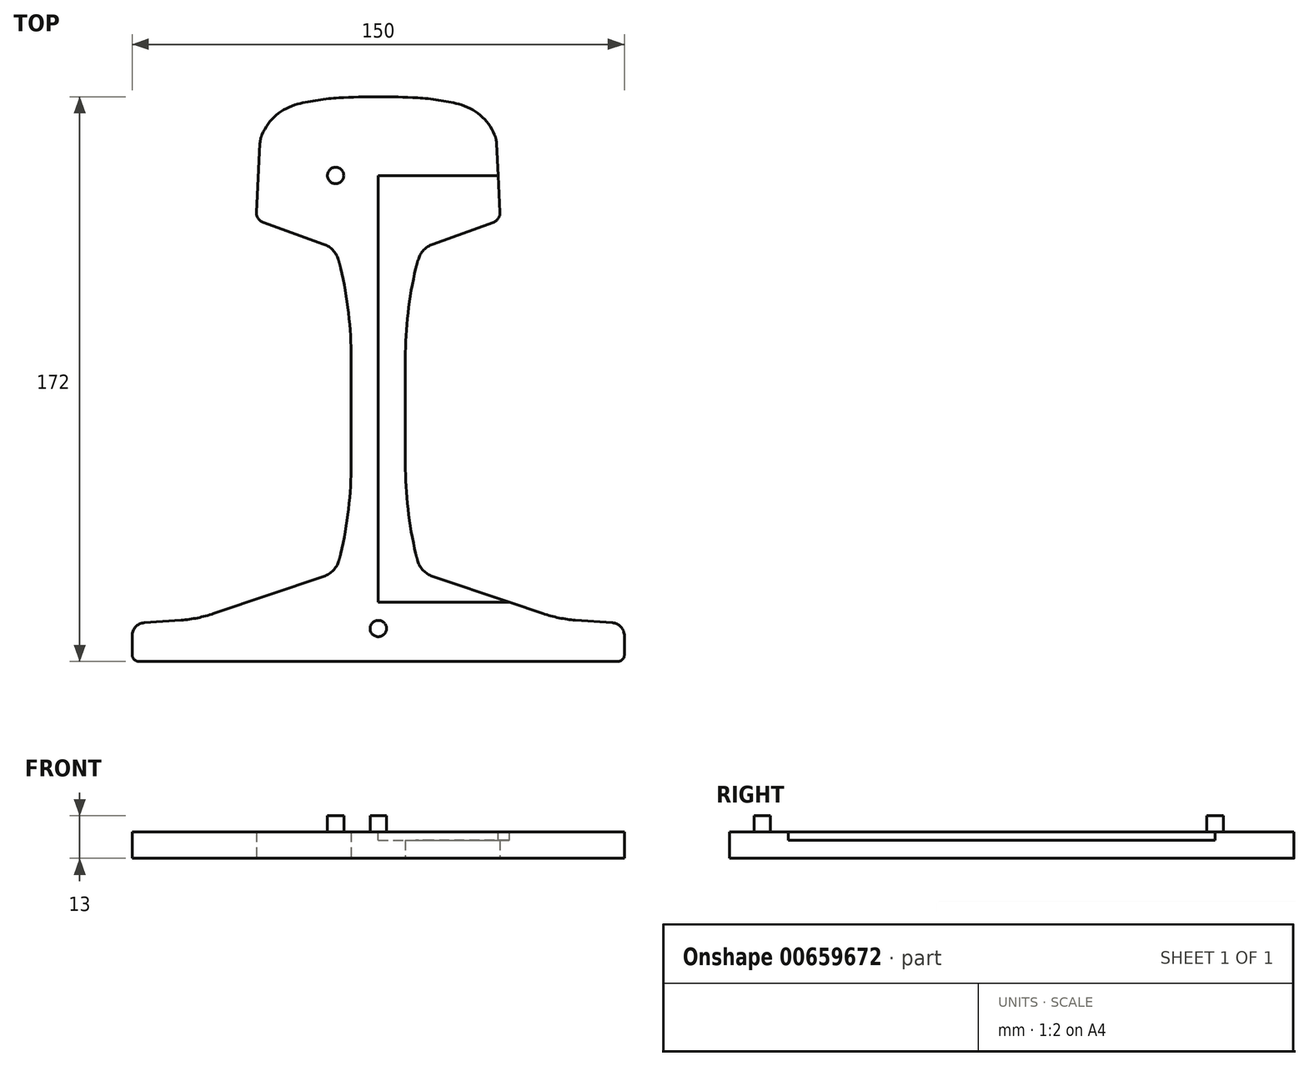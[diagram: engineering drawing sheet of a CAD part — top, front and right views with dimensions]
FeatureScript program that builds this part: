
annotation { "Feature Type Name" : "Feature", "Feature Type Description" : "" }
export const myFeature = defineFeature(function(context is Context, id is Id, definition is map)
    precondition{}
    {
        {
            var Q0;
            Q0=qCreatedBy(makeId("Top.planeOp"),FACE);
            var sketch = newSketch(context, id + "F0", { "sketchPlane" : qUnion([Q0])});
            skPoint(sketch, "E0.middle", {"position": v(0, 0) * mm});
            skLineSegment(sketch, "E1", {"start": v(0, 0) * mm, "end": v(73, 0) * mm});
            skLineSegment(sketch, "E2", {"start": v(75, 2) * mm, "end": v(75, 7.78) * mm});
            skLineSegment(sketch, "E3", {"start": v(0, 0) * mm, "end": v(0, 172) * mm, "construction": true});
            skLineSegment(sketch, "E4", {"start": v(71.28, 11.77) * mm, "end": v(60.1, 12.56) * mm});
            skLineSegment(sketch, "E5", {"start": v(50.15, 14.56) * mm, "end": v(16.5, 25.93) * mm});
            skPoint(sketch, "E6.orphan", {"position": v(0, 16.86) * mm});
            skPoint(sketch, "E7.visualSharp", {"position": v(75, 11.5) * mm});
            skArc(sketch, "E7.filletArc", {"start": v(75, 7.78) * mm, "mid": v(73.93, 10.5) * mm, "end": v(71.28, 11.77) * mm});
            skPoint(sketch, "E8.visualSharp", {"position": v(75, 0) * mm});
            skArc(sketch, "E8.filletArc", {"start": v(73, 0) * mm, "mid": v(74.41, 0.59) * mm, "end": v(75, 2) * mm});
            skPoint(sketch, "E9.visualSharp", {"position": v(55, 12.93) * mm});
            skArc(sketch, "E9.filletArc", {"start": v(50.15, 14.56) * mm, "mid": v(55.06, 13.25) * mm, "end": v(60.1, 12.56) * mm});
            skArc(sketch, "E10", {"start": v(8.25, 60.25) * mm, "mid": v(9.05, 46.4) * mm, "end": v(11.45, 32.72) * mm});
            skArc(sketch, "E11", {"start": v(11.45, 32.72) * mm, "mid": v(11.73, 31.61) * mm, "end": v(12.05, 30.51) * mm});
            skPoint(sketch, "E12.orphan", {"position": v(0, 31.5) * mm});
            skLineSegment(sketch, "E13", {"start": v(16.5, 127) * mm, "end": v(35.13, 133.78) * mm});
            skLineSegment(sketch, "E14", {"start": v(37.1, 136.75) * mm, "end": v(36.06, 157.7) * mm});
            skLineSegment(sketch, "E15", {"start": v(37.22, 134.53) * mm, "end": v(37.22, 152.14) * mm, "construction": true});
            skArc(sketch, "E16", {"start": v(24.5, 169.74) * mm, "mid": v(31.09, 166.37) * mm, "end": v(35.44, 160.4) * mm});
            skLineSegment(sketch, "E17", {"start": v(0, 172) * mm, "end": v(-54.44, 172) * mm, "construction": true});
            skArc(sketch, "E18", {"start": v(12, 171.64) * mm, "mid": v(6, 171.9) * mm, "end": v(0, 172) * mm});
            skArc(sketch, "E19", {"start": v(12, 171.64) * mm, "mid": v(18.3, 170.97) * mm, "end": v(24.5, 169.74) * mm});
            skPoint(sketch, "E20.visualSharp", {"position": v(36, 158.86) * mm});
            skArc(sketch, "E20.filletArc", {"start": v(36.06, 157.7) * mm, "mid": v(35.87, 159.07) * mm, "end": v(35.44, 160.4) * mm});
            skPoint(sketch, "E21.visualSharp", {"position": v(37.22, 134.53) * mm});
            skArc(sketch, "E22", {"start": v(11.45, 119.78) * mm, "mid": v(9.05, 106.1) * mm, "end": v(8.25, 92.25) * mm});
            skLineSegment(sketch, "E23", {"start": v(0, 121) * mm, "end": v(67.7, 121) * mm, "construction": true});
            skArc(sketch, "E24.filletArc", {"start": v(35.13, 133.78) * mm, "mid": v(36.6, 134.94) * mm, "end": v(37.1, 136.75) * mm});
            skArc(sketch, "E25", {"start": v(12.24, 122.6) * mm, "mid": v(11.81, 121.2) * mm, "end": v(11.45, 119.78) * mm});
            skPoint(sketch, "E26.visualSharp", {"position": v(13.51, 125.91) * mm});
            skArc(sketch, "E26.filletArc", {"start": v(16.5, 127) * mm, "mid": v(13.86, 125.29) * mm, "end": v(12.24, 122.6) * mm});
            skLineSegment(sketch, "E27", {"start": v(8.25, 92.25) * mm, "end": v(8.25, 60.25) * mm});
            skArc(sketch, "E28.MirrorCS", {"start": v(-12, 171.64) * mm, "mid": v(-18.3, 170.97) * mm, "end": v(-24.5, 169.74) * mm});
            skArc(sketch, "E29.MirrorCS", {"start": v(-12, 171.64) * mm, "mid": v(-6, 171.9) * mm, "end": v(0, 172) * mm});
            skArc(sketch, "E30.MirrorCS", {"start": v(-24.5, 169.74) * mm, "mid": v(-31.09, 166.37) * mm, "end": v(-35.44, 160.4) * mm});
            skArc(sketch, "E31.MirrorCS", {"start": v(-36.06, 157.7) * mm, "mid": v(-35.87, 159.07) * mm, "end": v(-35.44, 160.4) * mm});
            skLineSegment(sketch, "E32.MirrorCS", {"start": v(-37.1, 136.75) * mm, "end": v(-36.06, 157.7) * mm});
            skArc(sketch, "E33.MirrorCS", {"start": v(-35.13, 133.78) * mm, "mid": v(-36.6, 134.94) * mm, "end": v(-37.1, 136.75) * mm});
            skLineSegment(sketch, "E34.MirrorCS", {"start": v(-16.5, 127) * mm, "end": v(-35.13, 133.78) * mm});
            skArc(sketch, "E35.MirrorCS", {"start": v(-16.5, 127) * mm, "mid": v(-13.86, 125.29) * mm, "end": v(-12.24, 122.6) * mm});
            skArc(sketch, "E36.MirrorCS", {"start": v(-12.24, 122.6) * mm, "mid": v(-11.81, 121.2) * mm, "end": v(-11.45, 119.78) * mm});
            skArc(sketch, "E37.MirrorCS", {"start": v(-11.45, 119.78) * mm, "mid": v(-9.05, 106.1) * mm, "end": v(-8.25, 92.25) * mm});
            skLineSegment(sketch, "E38.MirrorCS", {"start": v(-8.25, 92.25) * mm, "end": v(-8.25, 60.25) * mm});
            skArc(sketch, "E39.MirrorCS", {"start": v(-8.25, 60.25) * mm, "mid": v(-9.05, 46.4) * mm, "end": v(-11.45, 32.72) * mm});
            skArc(sketch, "E40.MirrorCS", {"start": v(-11.45, 32.72) * mm, "mid": v(-11.73, 31.61) * mm, "end": v(-12.05, 30.51) * mm});
            skLineSegment(sketch, "E41.MirrorCS", {"start": v(-50.15, 14.56) * mm, "end": v(-16.5, 25.93) * mm});
            skArc(sketch, "E42.MirrorCS", {"start": v(-50.15, 14.56) * mm, "mid": v(-55.06, 13.25) * mm, "end": v(-60.1, 12.56) * mm});
            skLineSegment(sketch, "E43.MirrorCS", {"start": v(-71.28, 11.77) * mm, "end": v(-60.1, 12.56) * mm});
            skPoint(sketch, "E44.MirrorP", {"position": v(-75, 11.5) * mm});
            skArc(sketch, "E45.MirrorCS", {"start": v(-75, 7.78) * mm, "mid": v(-73.93, 10.5) * mm, "end": v(-71.28, 11.77) * mm});
            skLineSegment(sketch, "E46.MirrorCS", {"start": v(-75, 2) * mm, "end": v(-75, 7.78) * mm});
            skArc(sketch, "E47.MirrorCS", {"start": v(-73, 0) * mm, "mid": v(-74.41, 0.59) * mm, "end": v(-75, 2) * mm});
            skLineSegment(sketch, "E48.MirrorCS", {"start": v(0, 0) * mm, "end": v(-73, 0) * mm});
            skPoint(sketch, "E49.visualSharp", {"position": v(13.33, 27) * mm});
            skArc(sketch, "E49.filletArc", {"start": v(12.05, 30.51) * mm, "mid": v(13.72, 27.68) * mm, "end": v(16.5, 25.93) * mm});
            skPoint(sketch, "E50.visualSharp", {"position": v(-13.33, 27) * mm});
            skArc(sketch, "E50.filletArc", {"start": v(-16.5, 25.93) * mm, "mid": v(-13.72, 27.68) * mm, "end": v(-12.05, 30.51) * mm});
            skSolve(sketch);
        }
        {
            var Q0;
            Q0=makeQuery(id+"F0.imprint","IMPRINT",FACE,{"disambiguationData":[TD([[makeQuery(id+"F0.imprint","IMPRINT",EDGE,{"derivedFrom":sQuery(id+"F0.wireOp",EDGE,"E1")}),1.0]])]});
            extrude(context, id + "F1", {"entities" : qUnion([Q0]), "depth" : 8 * mm, "offsetDistance" : 25 * mm});
        }
        {
            var Q0;
            Q0=makeQuery(id+"F1.opExtrude","CAP_FACE",FACE,{"disambiguationData":[OSD([sQuery(id+"F0.wireOp",EDGE,"E1"),sQuery(id+"F0.wireOp",EDGE,"E2"),sQuery(id+"F0.wireOp",EDGE,"E4"),sQuery(id+"F0.wireOp",EDGE,"E5"),sQuery(id+"F0.wireOp",EDGE,"E7.filletArc"),sQuery(id+"F0.wireOp",EDGE,"E8.filletArc"),sQuery(id+"F0.wireOp",EDGE,"E9.filletArc"),sQuery(id+"F0.wireOp",EDGE,"E10"),sQuery(id+"F0.wireOp",EDGE,"E11"),sQuery(id+"F0.wireOp",EDGE,"E13"),sQuery(id+"F0.wireOp",EDGE,"E14"),sQuery(id+"F0.wireOp",EDGE,"E16"),sQuery(id+"F0.wireOp",EDGE,"E18"),sQuery(id+"F0.wireOp",EDGE,"E19"),sQuery(id+"F0.wireOp",EDGE,"E20.filletArc"),sQuery(id+"F0.wireOp",EDGE,"E22"),sQuery(id+"F0.wireOp",EDGE,"E24.filletArc"),sQuery(id+"F0.wireOp",EDGE,"E25"),sQuery(id+"F0.wireOp",EDGE,"E26.filletArc"),sQuery(id+"F0.wireOp",EDGE,"E27"),sQuery(id+"F0.wireOp",EDGE,"E28.MirrorCS"),sQuery(id+"F0.wireOp",EDGE,"E29.MirrorCS"),sQuery(id+"F0.wireOp",EDGE,"E30.MirrorCS"),sQuery(id+"F0.wireOp",EDGE,"E31.MirrorCS"),sQuery(id+"F0.wireOp",EDGE,"E32.MirrorCS"),sQuery(id+"F0.wireOp",EDGE,"E33.MirrorCS"),sQuery(id+"F0.wireOp",EDGE,"E34.MirrorCS"),sQuery(id+"F0.wireOp",EDGE,"E35.MirrorCS"),sQuery(id+"F0.wireOp",EDGE,"E36.MirrorCS"),sQuery(id+"F0.wireOp",EDGE,"E37.MirrorCS"),sQuery(id+"F0.wireOp",EDGE,"E38.MirrorCS"),sQuery(id+"F0.wireOp",EDGE,"E39.MirrorCS"),sQuery(id+"F0.wireOp",EDGE,"E40.MirrorCS"),sQuery(id+"F0.wireOp",EDGE,"E41.MirrorCS"),sQuery(id+"F0.wireOp",EDGE,"E42.MirrorCS"),sQuery(id+"F0.wireOp",EDGE,"E43.MirrorCS"),sQuery(id+"F0.wireOp",EDGE,"E45.MirrorCS"),sQuery(id+"F0.wireOp",EDGE,"E46.MirrorCS"),sQuery(id+"F0.wireOp",EDGE,"E47.MirrorCS"),sQuery(id+"F0.wireOp",EDGE,"E48.MirrorCS"),sQuery(id+"F0.wireOp",EDGE,"E49.filletArc"),sQuery(id+"F0.wireOp",EDGE,"E50.filletArc")])],"isStart":false});
            var sketch = newSketch(context, id + "F2", { "sketchPlane" : qUnion([Q0])});
            skLineSegment(sketch, "E51.bottom", {"start": v(0, 148) * mm, "end": v(118.3, 148) * mm});
            skLineSegment(sketch, "E51.left", {"start": v(0, 148) * mm, "end": v(0, 18) * mm});
            skLineSegment(sketch, "E51.right", {"start": v(118.3, 148) * mm, "end": v(118.3, 18) * mm});
            skLineSegment(sketch, "E52", {"start": v(0, 18) * mm, "end": v(118.3, 18) * mm});
            skSolve(sketch);
        }
        {
            var Q0;
            Q0 = qSketchRegion(id + "F2", true);
            extrude(context, id + "F3", {"entities" : qUnion([Q0]), "operationType" : NewBodyOperationType.REMOVE, "oppositeDirection" : true, "depth" : 2.5 * mm, "offsetDistance" : 25 * mm});
        }
        {
            var Q0;
            Q0=makeQuery(id+"F1.opExtrude","CAP_FACE",FACE,{"disambiguationData":[OSD([sQuery(id+"F0.wireOp",EDGE,"E1"),sQuery(id+"F0.wireOp",EDGE,"E2"),sQuery(id+"F0.wireOp",EDGE,"E4"),sQuery(id+"F0.wireOp",EDGE,"E5"),sQuery(id+"F0.wireOp",EDGE,"E7.filletArc"),sQuery(id+"F0.wireOp",EDGE,"E8.filletArc"),sQuery(id+"F0.wireOp",EDGE,"E9.filletArc"),sQuery(id+"F0.wireOp",EDGE,"E10"),sQuery(id+"F0.wireOp",EDGE,"E11"),sQuery(id+"F0.wireOp",EDGE,"E13"),sQuery(id+"F0.wireOp",EDGE,"E14"),sQuery(id+"F0.wireOp",EDGE,"E16"),sQuery(id+"F0.wireOp",EDGE,"E18"),sQuery(id+"F0.wireOp",EDGE,"E19"),sQuery(id+"F0.wireOp",EDGE,"E20.filletArc"),sQuery(id+"F0.wireOp",EDGE,"E22"),sQuery(id+"F0.wireOp",EDGE,"E24.filletArc"),sQuery(id+"F0.wireOp",EDGE,"E25"),sQuery(id+"F0.wireOp",EDGE,"E26.filletArc"),sQuery(id+"F0.wireOp",EDGE,"E27"),sQuery(id+"F0.wireOp",EDGE,"E28.MirrorCS"),sQuery(id+"F0.wireOp",EDGE,"E29.MirrorCS"),sQuery(id+"F0.wireOp",EDGE,"E30.MirrorCS"),sQuery(id+"F0.wireOp",EDGE,"E31.MirrorCS"),sQuery(id+"F0.wireOp",EDGE,"E32.MirrorCS"),sQuery(id+"F0.wireOp",EDGE,"E33.MirrorCS"),sQuery(id+"F0.wireOp",EDGE,"E34.MirrorCS"),sQuery(id+"F0.wireOp",EDGE,"E35.MirrorCS"),sQuery(id+"F0.wireOp",EDGE,"E36.MirrorCS"),sQuery(id+"F0.wireOp",EDGE,"E37.MirrorCS"),sQuery(id+"F0.wireOp",EDGE,"E38.MirrorCS"),sQuery(id+"F0.wireOp",EDGE,"E39.MirrorCS"),sQuery(id+"F0.wireOp",EDGE,"E40.MirrorCS"),sQuery(id+"F0.wireOp",EDGE,"E41.MirrorCS"),sQuery(id+"F0.wireOp",EDGE,"E42.MirrorCS"),sQuery(id+"F0.wireOp",EDGE,"E43.MirrorCS"),sQuery(id+"F0.wireOp",EDGE,"E45.MirrorCS"),sQuery(id+"F0.wireOp",EDGE,"E46.MirrorCS"),sQuery(id+"F0.wireOp",EDGE,"E47.MirrorCS"),sQuery(id+"F0.wireOp",EDGE,"E48.MirrorCS"),sQuery(id+"F0.wireOp",EDGE,"E49.filletArc"),sQuery(id+"F0.wireOp",EDGE,"E50.filletArc")])],"isStart":false});
            var sketch = newSketch(context, id + "F4", { "sketchPlane" : qUnion([Q0])});
            skCircle(sketch, "E53", {"center": v(0, 10) * mm, "radius": 2.5 * mm});
            skCircle(sketch, "E54", {"center": v(-13, 148) * mm, "radius": 2.5 * mm});
            skSolve(sketch);
        }
        {
            var Q0;
            Q0 = qSketchRegion(id + "F4", true);
            extrude(context, id + "F5", {"entities" : qUnion([Q0]), "operationType" : NewBodyOperationType.ADD, "depth" : 5 * mm, "offsetDistance" : 25 * mm});
        }
    });
